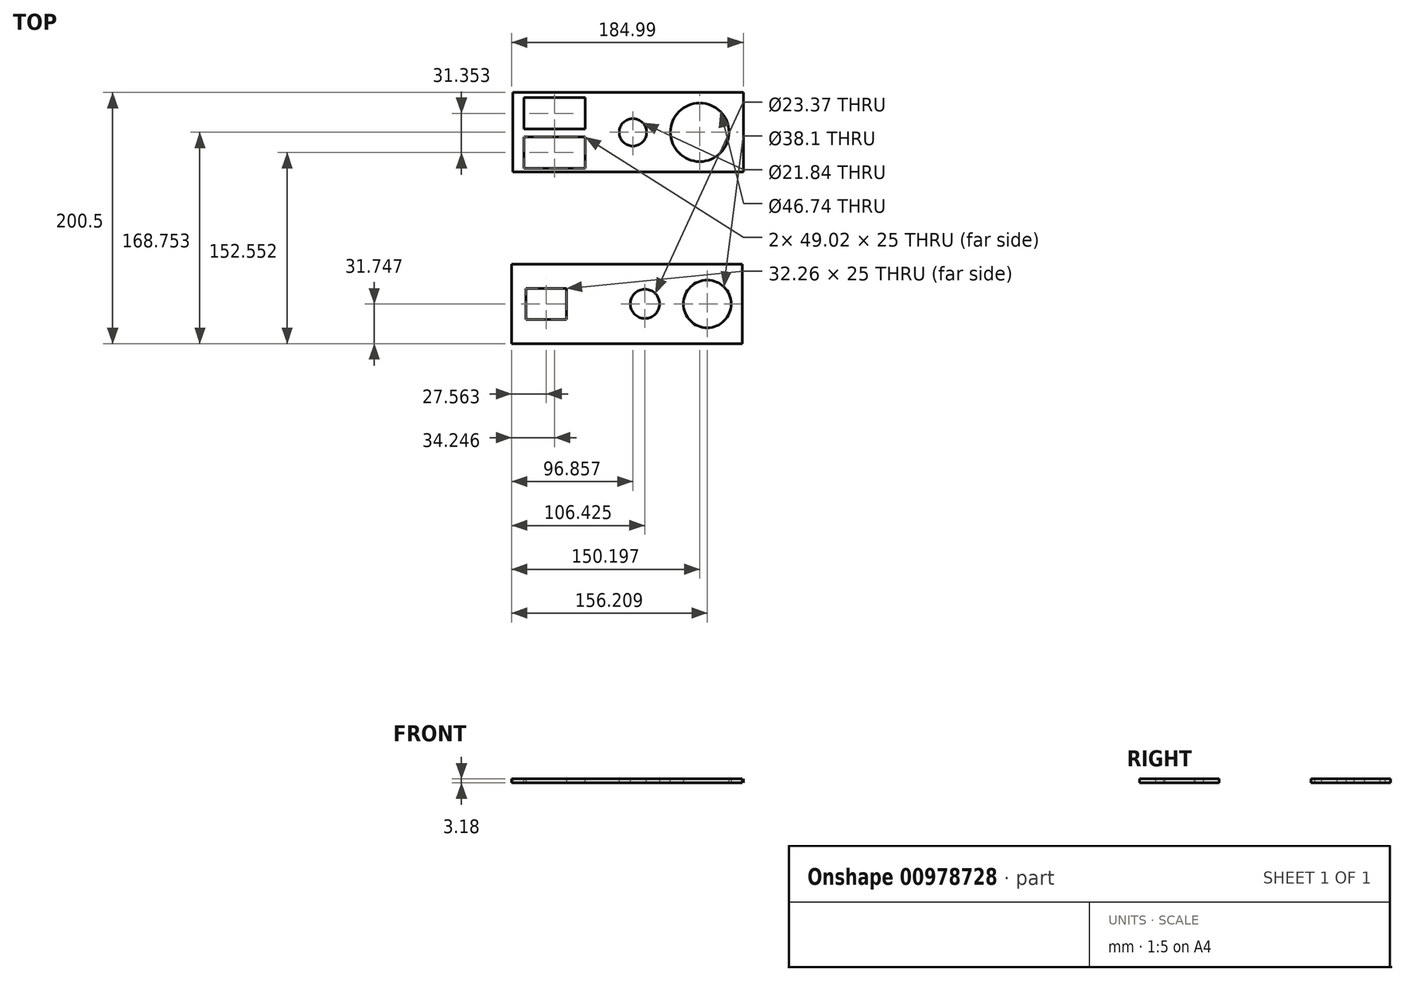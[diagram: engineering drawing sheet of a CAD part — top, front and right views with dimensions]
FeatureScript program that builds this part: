
annotation { "Feature Type Name" : "Feature", "Feature Type Description" : "" }
export const myFeature = defineFeature(function(context is Context, id is Id, definition is map)
    precondition{}
    {
        {
            var Q0;
            Q0=qCreatedBy(makeId("Top.planeOp"),FACE);
            var sketch = newSketch(context, id + "F0", { "sketchPlane" : qUnion([Q0])});
            skLineSegment(sketch, "E0.bottom", {"start": v(-82.79, -26.6) * mm, "end": v(101.36, -26.6) * mm});
            skLineSegment(sketch, "E0.top", {"start": v(-82.79, 36.9) * mm, "end": v(101.36, 36.9) * mm});
            skLineSegment(sketch, "E0.left", {"start": v(-82.79, -26.6) * mm, "end": v(-82.79, 36.9) * mm});
            skLineSegment(sketch, "E0.right", {"start": v(101.36, -26.6) * mm, "end": v(101.36, 36.9) * mm});
            skSolve(sketch);
        }
        {
            var Q0;
            Q0=makeQuery(id+"F0.imprint","IMPRINT",FACE,{"disambiguationData":[TD([[makeQuery(id+"F0.imprint","IMPRINT",EDGE,{"derivedFrom":sQuery(id+"F0.wireOp",EDGE,"E0.bottom")}),1.0]])]});
            extrude(context, id + "F1", {"entities" : qUnion([Q0]), "depth" : 3.17 * mm, "offsetDistance" : 25.4 * mm});
        }
        {
            var Q0;
            Q0=makeQuery(id+"F1.opExtrude","CAP_FACE",FACE,{"disambiguationData":[OSD([sQuery(id+"F0.wireOp",EDGE,"E0.bottom"),sQuery(id+"F0.wireOp",EDGE,"E0.top"),sQuery(id+"F0.wireOp",EDGE,"E0.left"),sQuery(id+"F0.wireOp",EDGE,"E0.right")])],"isStart":false});
            var sketch = newSketch(context, id + "F2", { "sketchPlane" : qUnion([Q0])});
            skLineSegment(sketch, "E1.bottom", {"start": v(-73.9, 32.8) * mm, "end": v(-24.87, 32.8) * mm});
            skLineSegment(sketch, "E1.top", {"start": v(-73.9, 7.8) * mm, "end": v(-24.87, 7.8) * mm});
            skLineSegment(sketch, "E1.left", {"start": v(-73.9, 32.8) * mm, "end": v(-73.9, 7.8) * mm});
            skLineSegment(sketch, "E1.right", {"start": v(-24.87, 32.8) * mm, "end": v(-24.87, 7.8) * mm});
            skLineSegment(sketch, "E2.bottom", {"start": v(-73.9, 1.44) * mm, "end": v(-24.87, 1.44) * mm});
            skLineSegment(sketch, "E2.top", {"start": v(-73.9, -23.56) * mm, "end": v(-24.87, -23.56) * mm});
            skLineSegment(sketch, "E2.left", {"start": v(-73.9, 1.44) * mm, "end": v(-73.9, -23.56) * mm});
            skLineSegment(sketch, "E2.right", {"start": v(-24.87, 1.44) * mm, "end": v(-24.87, -23.56) * mm});
            skLineSegment(sketch, "E3", {"start": v(-73.9, 36.9) * mm, "end": v(-73.9, -28.11) * mm, "construction": true});
            skCircle(sketch, "E4", {"center": v(66.57, 5.14) * mm, "radius": 23.37 * mm});
            skCircle(sketch, "E5", {"center": v(13.23, 5.14) * mm, "radius": 10.92 * mm});
            skLineSegment(sketch, "E6", {"start": v(101.36, 5.14) * mm, "end": v(-82.79, 5.14) * mm, "construction": true});
            skLineSegment(sketch, "E7", {"start": v(9.29, 36.9) * mm, "end": v(9.29, -26.6) * mm, "construction": true});
            skSolve(sketch);
        }
        {
            var Q0;
            Q0 = qSketchRegion(id + "F2", true);
            extrude(context, id + "F3", {"entities" : qUnion([Q0]), "operationType" : NewBodyOperationType.REMOVE, "oppositeDirection" : true, "depth" : 25.4 * mm, "offsetDistance" : 25.4 * mm});
        }
        {
            var Q0;
            Q0=qCreatedBy(makeId("Top.planeOp"),FACE);
            var sketch = newSketch(context, id + "F4", { "sketchPlane" : qUnion([Q0])});
            skLineSegment(sketch, "E8.bottom", {"start": v(-83.63, -100.11) * mm, "end": v(100.52, -100.11) * mm});
            skLineSegment(sketch, "E8.top", {"start": v(-83.63, -163.61) * mm, "end": v(100.52, -163.61) * mm});
            skLineSegment(sketch, "E8.left", {"start": v(-83.63, -100.11) * mm, "end": v(-83.63, -163.61) * mm});
            skLineSegment(sketch, "E8.right", {"start": v(100.52, -100.11) * mm, "end": v(100.52, -163.61) * mm});
            skSolve(sketch);
        }
        {
            var Q0;
            Q0 = qSketchRegion(id + "F4", true);
            extrude(context, id + "F5", {"entities" : qUnion([Q0]), "depth" : 3.17 * mm, "offsetDistance" : 25.4 * mm});
        }
        {
            var Q0;
            Q0=makeQuery(id+"F4.imprint","IMPRINT",FACE,{"disambiguationData":[TD([[makeQuery(id+"F4.imprint","IMPRINT",EDGE,{"derivedFrom":sQuery(id+"F4.wireOp",EDGE,"E8.bottom")}),-1.0]])]});
            var sketch = newSketch(context, id + "F6", { "sketchPlane" : qUnion([Q0])});
            skCircle(sketch, "E9", {"center": v(72.58, -131.86) * mm, "radius": 19.05 * mm});
            skLineSegment(sketch, "E10", {"start": v(-83.63, -131.86) * mm, "end": v(101.47, -131.86) * mm, "construction": true});
            skLineSegment(sketch, "E11", {"start": v(8.44, -163.61) * mm, "end": v(8.44, -100.11) * mm, "construction": true});
            skCircle(sketch, "E12", {"center": v(22.8, -131.86) * mm, "radius": 11.68 * mm});
            skLineSegment(sketch, "E13.bottom", {"start": v(-72.2, -119.36) * mm, "end": v(-39.94, -119.36) * mm});
            skLineSegment(sketch, "E13.top", {"start": v(-72.2, -144.36) * mm, "end": v(-39.94, -144.36) * mm});
            skLineSegment(sketch, "E13.left", {"start": v(-72.2, -119.36) * mm, "end": v(-72.2, -144.36) * mm});
            skLineSegment(sketch, "E13.right", {"start": v(-39.94, -119.36) * mm, "end": v(-39.94, -144.36) * mm});
            skPoint(sketch, "E14", {"position": v(-72.2, -131.86) * mm});
            skSolve(sketch);
        }
        {
            var Q0;
            Q0 = qSketchRegion(id + "F6", true);
            var Q1;
            Q1=makeQuery(id+"F5.opExtrude","CAP_FACE",FACE,{"disambiguationData":[OSD([sQuery(id+"F4.wireOp",EDGE,"E8.bottom"),sQuery(id+"F4.wireOp",EDGE,"E8.top"),sQuery(id+"F4.wireOp",EDGE,"E8.left"),sQuery(id+"F4.wireOp",EDGE,"E8.right")])],"isStart":false});
            extrude(context, id + "F7", {"entities" : qUnion([Q0]), "operationType" : NewBodyOperationType.REMOVE, "endBound" : BoundingType.UP_TO_SURFACE, "depth" : 25.4 * mm, "endBoundEntityFace" : qUnion([Q1]), "offsetDistance" : 25.4 * mm});
        }
    });
